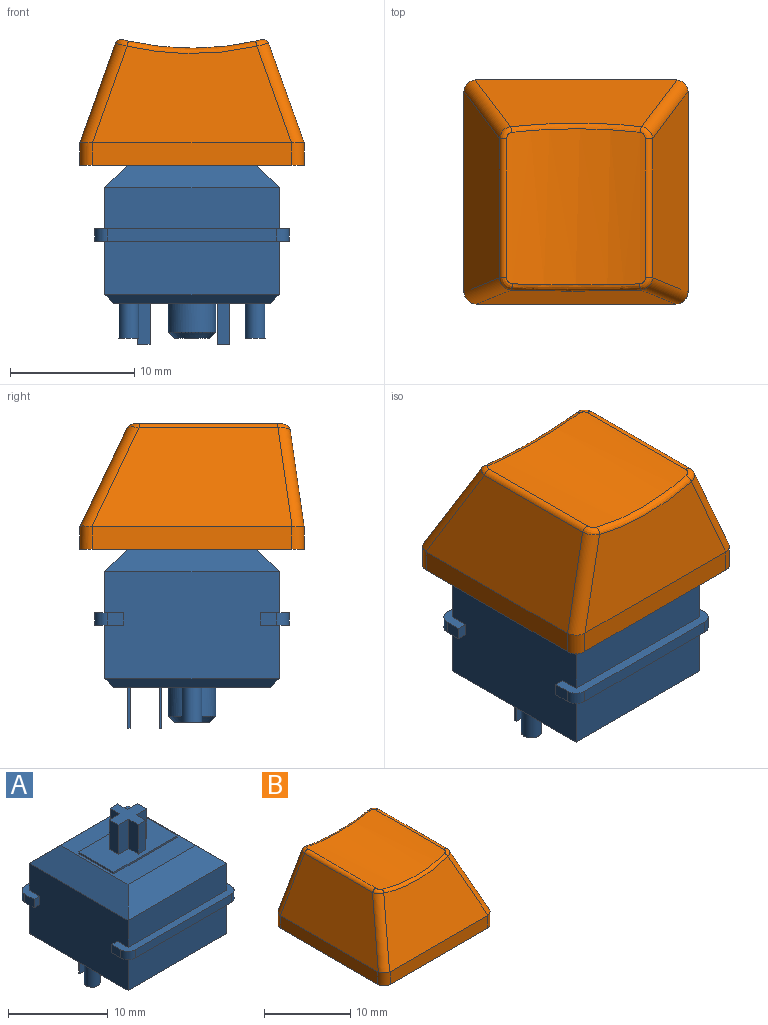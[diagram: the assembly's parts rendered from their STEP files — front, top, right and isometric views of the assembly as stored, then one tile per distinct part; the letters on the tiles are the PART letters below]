
ASSEMBLY  parts=2 mates=1
PART A: 69 faces, bbox 15.6x15.6x18.6 mm
  f0: plane 15.6x2.3mm, normal (0,0,-1), area 14.4mm2, adj f2,f3,f28,f30,f35,f60,f62,f63
  f1: plane 15.6x2.3mm, normal (0,0,-1), area 14.4mm2, adj f28,f30,f33,f34,f36,f59,f61,f64
  f2: plane 1.3x1mm, normal (1,0,0), area 1.3mm2, adj f0,f32,f62,f66
  f3: plane 1.3x1mm, normal (-1,0,0), area 1.3mm2, adj f0,f32,f63,f68
  f4: plane 15.6x2.3mm, normal (0,0,1), area 14.4mm2, adj f28,f30,f31,f33,f34,f36,f61,f64
  f5: plane 14x2.2mm, normal (-0.71,0,0.71), area 36.7mm2, adj f6,f7,f26,f30
  f6: plane 14x2.2mm, normal (0,-0.71,0.71), area 36.7mm2, adj f5,f7,f27,f31
  f7: plane 9.6x9.6mm, normal (0,0,1), area 47.2mm2, adj f5,f6,f8,f9,f10,f11,f26,f27
  f8: plane 5x0.2mm, normal (1,0,0), area 1mm2, adj f7,f9,f11,f12
  f9: plane 9x0.2mm, normal (0,1,0), area 1.8mm2, adj f7,f8,f10,f12
  f10: plane 5x0.2mm, normal (-1,0,0), area 1mm2, adj f7,f9,f11,f12
  f11: plane 9x0.2mm, normal (0,-1,0), area 1.8mm2, adj f7,f8,f10,f12
  f12: plane 9x5mm, normal (0,0,1), area 36.9mm2, adj f8,f9,f10,f11,f13,f14,f15,f16
  f13: plane 3.6x1.35mm, normal (1,0,0), area 4.9mm2, adj f12,f14,f24,f25
  f14: plane 3.6x1.08mm, normal (0,1,0), area 3.9mm2, adj f12,f13,f15,f25
  f15: plane 3.6x1.35mm, normal (-1,0,0), area 4.9mm2, adj f12,f14,f16,f25
  f16: plane 3.6x1.46mm, normal (0,1,0), area 5.3mm2, adj f12,f15,f17,f25
  f17: plane 3.6x1.3mm, normal (-1,0,0), area 4.7mm2, adj f12,f16,f18,f25
  f18: plane 3.6x1.46mm, normal (0,-1,0), area 5.3mm2, adj f12,f17,f19,f25
  f19: plane 3.6x1.35mm, normal (-1,0,0), area 4.9mm2, adj f12,f18,f20,f25
  f20: plane 3.6x1.08mm, normal (0,-1,0), area 3.9mm2, adj f12,f19,f21,f25
  f21: plane 3.6x1.35mm, normal (1,0,0), area 4.9mm2, adj f12,f20,f22,f25
  f22: plane 3.6x1.46mm, normal (0,-1,0), area 5.3mm2, adj f12,f21,f23,f25
  f23: plane 3.6x1.3mm, normal (1,0,0), area 4.7mm2, adj f12,f22,f24,f25
  f24: plane 3.6x1.46mm, normal (0,1,0), area 5.3mm2, adj f12,f13,f23,f25
  f25: plane 4x4mm, normal (0,0,1), area 8.1mm2, adj f13,f14,f15,f16,f17,f18,f19,f20
  f26: plane 14x2.2mm, normal (0,0.71,0.71), area 36.7mm2, adj f5,f7,f27,f29
  f27: plane 14x2.2mm, normal (0.71,0,0.71), area 36.7mm2, adj f6,f7,f26,f28
  f28: plane 14x8.6mm, normal (1,0,0), area 117.4mm2, adj f0,f1,f4,f27,f29,f31,f32,f55
  f29: plane 14x3.3mm, normal (0,1,0), area 46.2mm2, adj f26,f28,f30,f32
  f30: plane 14x8.6mm, normal (-1,0,0), area 117.4mm2, adj f0,f1,f4,f5,f29,f31,f32,f57
  f31: plane 14x3.3mm, normal (0,-1,0), area 46.2mm2, adj f4,f6,f28,f30
  f32: plane 15.6x2.3mm, normal (0,0,1), area 14.4mm2, adj f2,f3,f28,f29,f30,f35,f62,f63
  f33: plane 13.6x1mm, normal (0,-1,0), area 13.6mm2, adj f1,f4,f61,f64
  f34: plane 1.3x1mm, normal (1,0,0), area 1.3mm2, adj f1,f4,f61,f65
  f35: plane 13.6x1mm, normal (0,1,0), area 13.6mm2, adj f0,f32,f62,f63
  f36: plane 1.3x1mm, normal (-1,0,0), area 1.3mm2, adj f1,f4,f64,f67
  f37: plane 2.85x2.85mm, normal (0,0,-1), area 6.4mm2, adj f38
  f38: cone r=1.43mm half-angle=45deg, axis (0,0,1), area 7.4mm2, adj f37,f43
  f39: plane 1x0.2mm, normal (0,0,-1), area 0.2mm2, adj f44,f45,f46,f47
  f40: plane 1x0.2mm, normal (0,0,-1), area 0.2mm2, adj f48,f49,f50,f51
  f41: plane 1.6x1.6mm, normal (0,0,-1), area 2mm2, adj f52
  f42: plane 1.6x1.6mm, normal (0,0,-1), area 2mm2, adj f53
  f43: cylinder r=1.93mm len=3.85mm, axis (0,0,1), area 27.8mm2, adj f38,f54
  f44: plane 3.3x0.2mm, normal (-1,0,0), area 0.7mm2, adj f39,f45,f47,f54
  f45: plane 3.3x1mm, normal (0,1,0), area 3.3mm2, adj f39,f44,f46,f54
  f46: plane 3.3x0.2mm, normal (1,0,0), area 0.7mm2, adj f39,f45,f47,f54
  f47: plane 3.3x1mm, normal (0,-1,0), area 3.3mm2, adj f39,f44,f46,f54
  f48: plane 3.3x0.2mm, normal (-1,0,0), area 0.7mm2, adj f40,f49,f51,f54
  f49: plane 3.3x1mm, normal (0,1,0), area 3.3mm2, adj f40,f48,f50,f54
  f50: plane 3.3x0.2mm, normal (1,0,0), area 0.7mm2, adj f40,f49,f51,f54
  f51: plane 3.3x1mm, normal (0,-1,0), area 3.3mm2, adj f40,f48,f50,f54
  f52: cylinder r=0.8mm len=2.8mm, axis (0,0,1), area 14.1mm2, adj f41,f54
  f53: cylinder r=0.8mm len=2.8mm, axis (0,0,1), area 14.1mm2, adj f42,f54
  f54: plane 12.6x12.6mm, normal (0,0,-1), area 142.7mm2, adj f43,f44,f45,f46,f47,f48,f49,f50
  f55: plane 14x0.7mm, normal (0.71,0,-0.71), area 13.2mm2, adj f28,f54,f56,f58
  f56: plane 14x0.7mm, normal (0,0.71,-0.71), area 13.2mm2, adj f54,f55,f57,f60
  f57: plane 14x0.7mm, normal (-0.71,0,-0.71), area 13.2mm2, adj f30,f54,f56,f58
  f58: plane 14x0.7mm, normal (0,-0.71,-0.71), area 13.2mm2, adj f54,f55,f57,f59
  f59: plane 14x4.3mm, normal (0,-1,0), area 60.2mm2, adj f1,f28,f30,f58
  f60: plane 14x4.3mm, normal (0,1,0), area 60.2mm2, adj f0,f28,f30,f56
  f61: cylinder r=1mm len=1mm, axis (0,0,-1), area 1.6mm2, adj f1,f4,f33,f34
  f62: cylinder r=1mm len=1mm, axis (0,0,1), area 1.6mm2, adj f0,f2,f32,f35
  f63: cylinder r=1mm len=1mm, axis (0,0,-1), area 1.6mm2, adj f0,f3,f32,f35
  f64: cylinder r=1mm len=1mm, axis (0,0,1), area 1.6mm2, adj f1,f4,f33,f36
  f65: plane 1x0.8mm, normal (0,1,0), area 0.8mm2, adj f1,f4,f28,f34
  f66: plane 1x0.8mm, normal (0,-1,0), area 0.8mm2, adj f0,f2,f28,f32
  f67: plane 1x0.8mm, normal (0,1,0), area 0.8mm2, adj f1,f4,f30,f36
  f68: plane 1x0.8mm, normal (0,-1,0), area 0.8mm2, adj f0,f3,f30,f32
PART B: 50 faces, bbox 18.1x18x10.2 mm
  f0: plane 18x18mm, normal (0,0,-1), area 67.1mm2, adj f1,f2,f3,f4,f10,f12,f14,f16
  f1: plane 16x1.8mm, normal (1,0,0), area 28.8mm2, adj f0,f8,f10,f16
  f2: plane 16x1.8mm, normal (0,1,0), area 28.8mm2, adj f0,f5,f14,f15,f16,f17
  f3: plane 16x1.8mm, normal (-1,0,0), area 28.8mm2, adj f0,f6,f12,f14
  f4: plane 16x1.8mm, normal (0,-1,0), area 28.8mm2, adj f0,f7,f10,f12
  f5: plane 15.98x7.76mm, normal (0,0.99,0.14), area 99.4mm2, adj f2,f15,f17,f20
  f6: plane 16.09x7.97mm, normal (-0.94,0,0.34), area 115.3mm2, adj f3,f12,f13,f14,f15,f19
  f7: plane 16.18x7.92mm, normal (0,-0.9,0.43), area 112.4mm2, adj f4,f10,f11,f12,f13,f23
  f8: plane 16.09x7.97mm, normal (0.94,0,0.34), area 115.3mm2, adj f1,f10,f11,f16,f17,f24
  f9: cylinder r=22.9mm len=12.55mm, axis (0,-1,0), area 139.2mm2, adj f18,f19,f20,f21,f22,f23,f24,f25
  f10: cylinder r=1mm len=1.87mm, axis (0,0,-1), area 2.9mm2, adj f0,f1,f4,f7,f8,f11
  f11: cylinder r=1mm len=8.25mm, axis (0.31,-0.41,-0.86), area 13.2mm2, adj f7,f8,f10,f25
  f12: cylinder r=1mm len=1.87mm, axis (0,0,1), area 2.9mm2, adj f0,f3,f4,f6,f7,f13
  f13: cylinder r=1mm len=8.25mm, axis (0.31,0.41,0.86), area 13.2mm2, adj f6,f7,f12,f21
  f14: cylinder r=1mm len=1.83mm, axis (0,0,-1), area 2.9mm2, adj f0,f2,f3,f6,f15
  f15: cylinder r=1mm len=8.19mm, axis (-0.33,0.13,-0.93), area 12.9mm2, adj f2,f5,f6,f14,f18
  f16: cylinder r=1mm len=1.83mm, axis (0,0,1), area 2.9mm2, adj f0,f1,f2,f8,f17
  f17: cylinder r=1mm len=8.19mm, axis (-0.33,-0.13,0.93), area 12.9mm2, adj f2,f5,f8,f16,f22
  f18: bspline ~1.24x1.22mm, area 0.9mm2, adj f9,f15,f19,f20
  f19: cylinder r=0.5mm len=11.16mm, axis (0,-1,0), area 8.2mm2, adj f6,f9,f18,f21
  f20: bspline ~10.43x1.01mm, area 7.4mm2, adj f5,f9,f18,f22
  f21: bspline ~1.23x1.15mm, area 0.7mm2, adj f9,f13,f19,f23
  f22: bspline ~1.24x1.22mm, area 0.9mm2, adj f9,f17,f20,f24
  f23: bspline ~10.53x0.87mm, area 5.9mm2, adj f7,f9,f21,f25
  f24: cylinder r=0.5mm len=11.16mm, axis (0,-1,0), area 8.2mm2, adj f8,f9,f22,f25
  f25: bspline ~1.23x1.15mm, area 0.7mm2, adj f9,f11,f23,f24
  f26: plane 16x1.63mm, normal (-1,0,0), area 26mm2, adj f0,f27,f29,f32,f33
  f27: plane 16x1.73mm, normal (0,-1,0), area 27.7mm2, adj f0,f26,f28,f30,f31,f33
  f28: plane 16x1.63mm, normal (1,0,0), area 26mm2, adj f0,f27,f29,f31,f32
  f29: plane 16x1.57mm, normal (0,1,0), area 25.2mm2, adj f0,f26,f28,f32
  f30: plane 15.93x7.28mm, normal (0,-0.99,-0.14), area 93.6mm2, adj f27,f31,f33,f34
  f31: plane 15.98x7.38mm, normal (0.94,0,-0.34), area 107.4mm2, adj f27,f28,f30,f32,f34
  f32: plane 16x7.44mm, normal (0,0.9,-0.43), area 105.4mm2, adj f26,f28,f29,f31,f33,f34
  f33: plane 15.98x7.38mm, normal (-0.94,0,-0.34), area 107.4mm2, adj f26,f27,f30,f32,f34
  f34: cylinder r=23.9mm len=11.8mm, axis (0,-1,0), area 102.5mm2, adj f30,f31,f32,f33,f46
  f35: plane 7.81x1.5mm, normal (-1,0,0), area 11.7mm2, adj f36,f44,f45,f49
  f36: plane 7.9x1.5mm, normal (0,-1,0), area 11.8mm2, adj f35,f37,f45,f49
  f37: plane 7.9x1.3mm, normal (-1,0,0), area 10.3mm2, adj f36,f38,f45,f49
  f38: plane 7.9x1.5mm, normal (0,1,0), area 11.8mm2, adj f37,f39,f45,f49
  f39: plane 7.81x1.5mm, normal (-1,0,0), area 11.7mm2, adj f38,f40,f45,f49
  f40: plane 7.81x1.3mm, normal (0,1,0), area 10.1mm2, adj f39,f41,f45,f49
  f41: plane 7.81x1.5mm, normal (1,0,0), area 11.7mm2, adj f40,f42,f45,f49
  f42: plane 7.9x1.5mm, normal (0,1,0), area 11.8mm2, adj f41,f43,f45,f49
  f43: plane 7.9x1.3mm, normal (1,0,0), area 10.3mm2, adj f42,f45,f47,f49
  f44: plane 7.81x1.3mm, normal (0,-1,0), area 10.1mm2, adj f35,f45,f48,f49
  f45: plane 5.5x5.5mm, normal (0,0,-1), area 14.3mm2, adj f35,f36,f37,f38,f39,f40,f41,f42
  f46: cylinder r=2.75mm len=7.96mm, axis (0,0,-1), area 136.1mm2, adj f34,f45
  f47: plane 7.9x1.5mm, normal (0,-1,0), area 11.8mm2, adj f43,f45,f48,f49
  f48: plane 7.81x1.5mm, normal (1,0,0), area 11.7mm2, adj f44,f45,f47,f49
  f49: cylinder r=23.9mm len=4.3mm, axis (0,-1,0), area 9.5mm2, adj f35,f36,f37,f38,f39,f40,f41,f42
PLACE A at identity fixed
PLACE B rot(axis=(0,0,1),180deg) t=(0,0,11.1)mm
MATE fastened B.f46 <-> A.f38  axis (0,0,-1) through (0,0,11.7)mm
